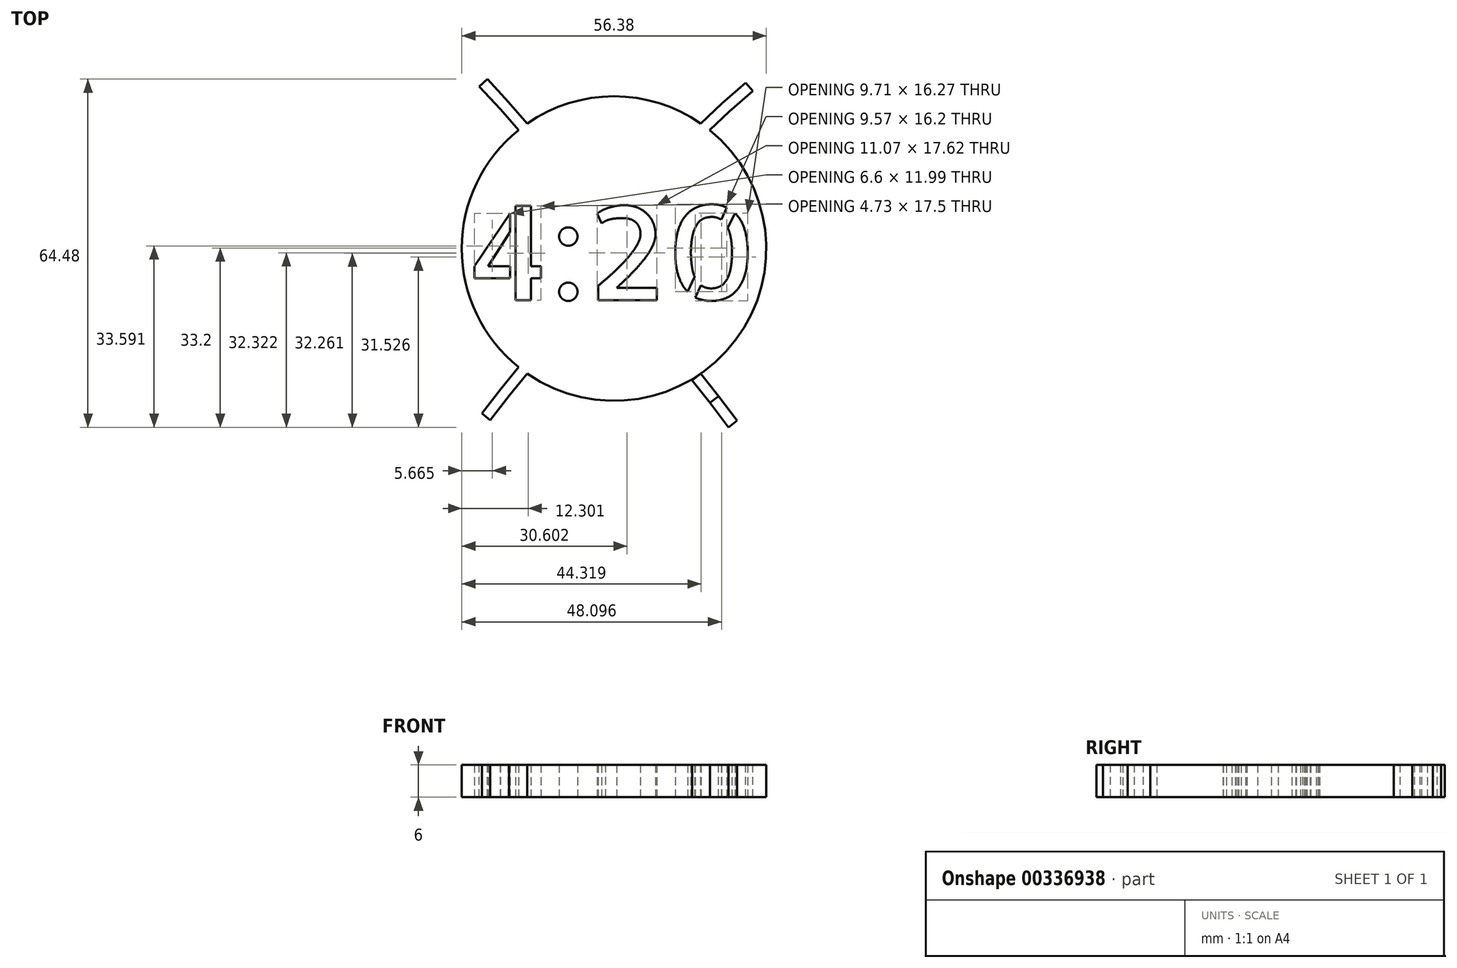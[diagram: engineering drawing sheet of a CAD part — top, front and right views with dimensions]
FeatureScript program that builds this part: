
annotation { "Feature Type Name" : "Feature", "Feature Type Description" : "" }
export const myFeature = defineFeature(function(context is Context, id is Id, definition is map)
    precondition{}
    {
        {
            var Q0;
            Q0=qCreatedBy(makeId("Top.planeOp"),FACE);
            var sketch = newSketch(context, id + "F0", { "sketchPlane" : qUnion([Q0])});
            skCircle(sketch, "E0", {"center": v(0, 0) * mm, "radius": 39.18 * mm});
            skCircle(sketch, "E1", {"center": v(0, 0) * mm, "radius": 33.49 * mm});
            skCircle(sketch, "E2", {"center": v(0, 0) * mm, "radius": 28.2 * mm});
            skLineSegment(sketch, "E3", {"start": v(0, 39.18) * mm, "end": v(0, 72.64) * mm});
            skText(sketch, "E4", { "text": "4:20", "fontName": "AllertaStencil-Regular.ttf"});
            skLineSegment(sketch, "E5", {"start": v(-23.46, 31.38) * mm, "end": v(-19.58, 27.17) * mm});
            skLineSegment(sketch, "E6", {"start": v(-19.58, 27.17) * mm, "end": v(-16.07, 23.16) * mm});
            skLineSegment(sketch, "E7", {"start": v(16.07, 23.16) * mm, "end": v(20, 26.85) * mm});
            skLineSegment(sketch, "E8", {"start": v(20, 26.85) * mm, "end": v(24.37, 30.68) * mm});
            skLineSegment(sketch, "E9", {"start": v(-16.07, -23.16) * mm, "end": v(-19.4, -27.3) * mm});
            skLineSegment(sketch, "E10", {"start": v(-19.4, -27.3) * mm, "end": v(-22.92, -31.78) * mm});
            skLineSegment(sketch, "E11", {"start": v(16.07, -23.16) * mm, "end": v(19.34, -27.34) * mm});
            skLineSegment(sketch, "E12", {"start": v(19.34, -27.34) * mm, "end": v(22.8, -31.87) * mm});
            const initialGuessF0  = {"E4": [-0.02673, -0.00959, 1, 0, 0.01751]};
            skSetInitialGuess(sketch, initialGuessF0);
            skSolve(sketch);
        }
        {
            var Q0;
            Q0=sQuery(id+"F0.wireOp",EDGE,"E0");
            extrude(context, id + "F1", {"bodyType" : ToolBodyType.SURFACE, "surfaceEntities" : qUnion([Q0]), "depth" : 6 * mm});
        }
        {
            var Q0;
            Q0=sQuery(id+"F0.wireOp",EDGE,"E1");
            extrude(context, id + "F2", {"bodyType" : ToolBodyType.SURFACE, "surfaceEntities" : qUnion([Q0]), "depth" : 6 * mm});
        }
        {
            var Q0;
            Q0=sQuery(id+"F0.wireOp",EDGE,"E2");
            extrude(context, id + "F3", {"bodyType" : ToolBodyType.SURFACE, "surfaceEntities" : qUnion([Q0]), "depth" : 6 * mm});
        }
        {
            var Q0;
            Q0=makeQuery(id+"F0.imprint","IMPRINT",FACE,{"disambiguationData":[TD([[makeQuery(id+"F0.imprint","IMPRINT",EDGE,{"derivedFrom":sQuery(id+"F0.wireOp",EDGE,"E2")}),1.0]])]});
            extrude(context, id + "F4", {"entities" : qUnion([Q0]), "depth" : 6 * mm});
        }
        {
            var Q0;
            Q0=makeQuery(id+"F0.imprint","IMPRINT",FACE,{"disambiguationData":[TD([[makeQuery(id+"F0.imprint","IMPRINT",EDGE,{"derivedFrom":sQuery(id+"F0.wireOp",EDGE,"E2")}),1.0]])]});
            extrude(context, id + "F5", {"entities" : qUnion([Q0]), "operationType" : NewBodyOperationType.ADD, "depth" : 6 * mm});
        }
        {
            var Q0;
            Q0=sQuery(id+"F0.wireOp",EDGE,"E5");
            var Q1;
            Q1=sQuery(id+"F0.wireOp",EDGE,"E6");
            var Q2;
            Q2=sQuery(id+"F0.wireOp",EDGE,"E7");
            var Q3;
            Q3=sQuery(id+"F0.wireOp",EDGE,"E8");
            extrude(context, id + "F6", {"bodyType" : ToolBodyType.SURFACE, "surfaceEntities" : qUnion([Q0, Q1, Q2, Q3]), "depth" : 6 * mm});
        }
        {
            var Q0;
            Q0=sQuery(id+"F0.wireOp",EDGE,"E11");
            var Q1;
            Q1=sQuery(id+"F0.wireOp",EDGE,"E12");
            var Q2;
            Q2=sQuery(id+"F0.wireOp",EDGE,"E9");
            var Q3;
            Q3=sQuery(id+"F0.wireOp",EDGE,"E10");
            extrude(context, id + "F7", {"bodyType" : ToolBodyType.SURFACE, "surfaceEntities" : qUnion([Q0, Q1, Q2, Q3]), "depth" : 6 * mm});
        }
        {
            var Q0;
            Q0=makeQuery(id+"F7.opExtrude","SWEPT_FACE",FACE,{"disambiguationData":[OSD([sQuery(id+"F0.wireOp",EDGE,"E11")])]});
            var Q1;
            Q1=makeQuery(id+"F7.opExtrude","SWEPT_FACE",FACE,{"disambiguationData":[OSD([sQuery(id+"F0.wireOp",EDGE,"E12")])]});
            extrude(context, id + "F8", {"entities" : qUnion([Q0, Q1]), "depth" : 2 * mm});
        }
        {
            var Q0;
            Q0=makeQuery(id+"F7.opExtrude","SWEPT_FACE",FACE,{"disambiguationData":[OSD([sQuery(id+"F0.wireOp",EDGE,"E9")])]});
            var Q1;
            Q1=makeQuery(id+"F7.opExtrude","SWEPT_FACE",FACE,{"disambiguationData":[OSD([sQuery(id+"F0.wireOp",EDGE,"E10")])]});
            extrude(context, id + "F9", {"entities" : qUnion([Q0, Q1]), "operationType" : NewBodyOperationType.ADD, "depth" : 2 * mm});
        }
        {
            var Q0;
            Q0=makeQuery(id+"F6.opExtrude","SWEPT_FACE",FACE,{"disambiguationData":[OSD([sQuery(id+"F0.wireOp",EDGE,"E5")])]});
            var Q1;
            Q1=makeQuery(id+"F6.opExtrude","SWEPT_FACE",FACE,{"disambiguationData":[OSD([sQuery(id+"F0.wireOp",EDGE,"E6")])]});
            extrude(context, id + "F10", {"entities" : qUnion([Q0, Q1]), "operationType" : NewBodyOperationType.ADD, "depth" : 2 * mm});
        }
        {
            var Q0;
            Q0=makeQuery(id+"F6.opExtrude","SWEPT_FACE",FACE,{"disambiguationData":[OSD([sQuery(id+"F0.wireOp",EDGE,"E8")])]});
            var Q1;
            Q1=makeQuery(id+"F6.opExtrude","SWEPT_FACE",FACE,{"disambiguationData":[OSD([sQuery(id+"F0.wireOp",EDGE,"E7")])]});
            extrude(context, id + "F11", {"entities" : qUnion([Q0, Q1]), "operationType" : NewBodyOperationType.ADD, "depth" : 2 * mm});
        }
    });
